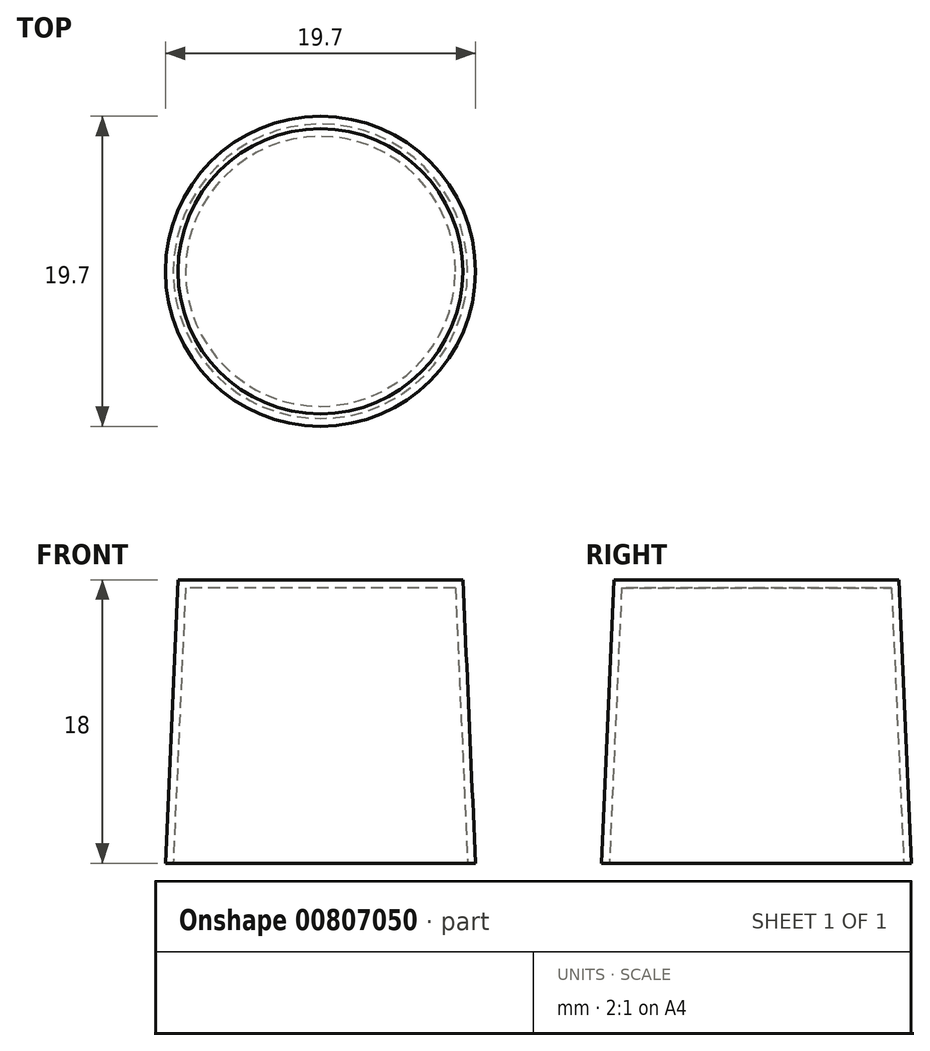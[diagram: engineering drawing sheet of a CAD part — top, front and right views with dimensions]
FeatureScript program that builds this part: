
annotation { "Feature Type Name" : "Feature", "Feature Type Description" : "" }
export const myFeature = defineFeature(function(context is Context, id is Id, definition is map)
    precondition{}
    {
        {
            assignVariable(context, id + "F0", {"name" : "h", "anyValue" : 18});
        }
        {
            var Q0;
            Q0=qCreatedBy(makeId("Top.planeOp"),FACE);
            var sketch = newSketch(context, id + "F1", { "sketchPlane" : qUnion([Q0])});
            skCircle(sketch, "E0", {"center": v(0, 0) * mm, "radius": 9.05 * mm});
            skSolve(sketch);
        }
        {
            var Q0;
            Q0=qCreatedBy(makeId("Top.planeOp"),FACE);
            cPlane(context, id + "F2", {"entities" : qUnion([Q0]), "cplaneType" : CPlaneType.OFFSET, "offset" : (getVariable(context, 'h')) * mm, "oppositeDirection" : true, "width" : 150 * mm, "height" : 150 * mm});
        }
        {
            var Q0;
            Q0=qCreatedBy(id+"F2.planeOp",FACE);
            var sketch = newSketch(context, id + "F3", { "sketchPlane" : qUnion([Q0])});
            skCircle(sketch, "E1", {"center": v(0, 0) * mm, "radius": 9.85 * mm});
            skSolve(sketch);
        }
        {
            var Q0;
            Q0=makeQuery(id+"F1.imprint","IMPRINT",FACE,{"disambiguationData":[TD([[makeQuery(id+"F1.imprint","IMPRINT",EDGE,{"derivedFrom":sQuery(id+"F1.wireOp",EDGE,"E0")}),1.0]])]});
            var Q1;
            Q1=makeQuery(id+"F3.imprint","IMPRINT",FACE,{"disambiguationData":[TD([[makeQuery(id+"F3.imprint","IMPRINT",EDGE,{"derivedFrom":sQuery(id+"F3.wireOp",EDGE,"E1")}),1.0]])]});
            loft(context, id + "F4", {"sheetProfilesArray" : [{ "sheetProfileEntities" : qUnion([Q0]) }, { "sheetProfileEntities" : qUnion([Q1]) }]});
        }
        {
            var Q0;
            Q0=makeQuery(id+"F4.opLoft","CAP_FACE",FACE,{"disambiguationData":[OSD([makeQuery(id+"F3.imprint","IMPRINT",FACE,{"disambiguationData":[TD([[makeQuery(id+"F3.imprint","IMPRINT",EDGE,{"derivedFrom":sQuery(id+"F3.wireOp",EDGE,"E1")}),1.0]])]})])],"isStart":true});
            shell(context, id + "F5", {"entities" : qUnion([Q0]), "thickness" : 0.5 * mm});
        }
    });
